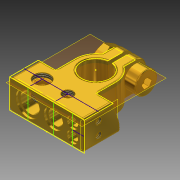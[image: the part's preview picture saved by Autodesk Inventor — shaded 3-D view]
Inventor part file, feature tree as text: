
AUTODESK INVENTOR PART (.ipt)
format: ipt  version: 2014 (Build 180170000, 170)  size: 792,576 bytes
history: native  units: in
note: dims shown in document units (in); Inventor stores cm internally (conversion verified against a paired STEP export)
features: sketch x14, projected_geometry x13, fillet x11, extrude x9, hole x7, other x6, chamfer x4, plane x3, surface_op x2, thread x2, mirror x1
ambient origin geometry x8: Origin, YZ Plane, XZ Plane, XY Plane, X Axis, Y Axis, Z Axis, Center Point
bodies: Solid1 (feature_tree)
feature tree (72):
  sketch  "Sketch1"  dims[d0=0.125in d2=0.375in]
  sketch  "Sketch2"  dims[d3=0.625in d4=0.5in d5=0.125in]
  plane  "Work Plane1"
  extrude  "Extrusion1"  Depth=0.125in
  surface_op  "Sculpt1"
  hole  "Hole1"  [1 undecoded]
  fillet  "Fillet1"  Radius=0.125in
  sketch  "Sketch4"  dims[d10=0.125in d11=1.0in d12=0.0in]
  hole  "Hole2"  [1 undecoded]
  hole  "Hole3"  [1 undecoded]
  hole  "Hole4"  [1 undecoded]
  extrude  "Extrusion3"  Depth=0.05in
  extrude  "Extrusion4"  Depth=0.03in
  mirror  "Mirror1"
  sketch  "Sketch8"  dims[d30=0.32in d31=0.75in d32=0.375in d33=0.25in d34=0.5635in d35=0.5in d36=0.0in]
  hole  "Hole5"  [1 undecoded]
  hole  "Hole6"  [1 undecoded]
  hole  "Hole7"  [1 undecoded]
  fillet  "Fillet3"  Radius=0.075in
  fillet  "Fillet4"  Radius=0.075in
  fillet  "Fillet5"  Radius=0.025in
  fillet  "Fillet6"  Radius=0.025in
  fillet  "Fillet7"  Radius=0.05in
  fillet  "Fillet8"  Radius=0.025in
  surface_op  "Sculpt2"
  extrude  "Extrusion5"  Depth=0.125in TaperAngle=0.0deg
  fillet  "Fillet9"  Radius=0.125in
  extrude  "Extrusion6"  [1 undecoded]
  chamfer  "Chamfer1"  Distance=0.28in
  plane  "Work Plane2"
  extrude  "Extrusion7"  Depth=0.125in TaperAngle=0.0deg
  thread  "Thread1"  [1 undecoded]
  thread  "Thread2"  [1 undecoded]
  chamfer  "Chamfer2"  Distance=0.1in
  extrude  "Extrusion8"  Depth=0.125in
  fillet  "Fillet10"  Radius=0.025in
  fillet  "Fillet11"  [1 undecoded]
  plane  "Work Plane3"
  extrude  "Extrusion9"  Depth=0.125in TaperAngle=0.0deg
  extrude  "Extrusion10"  Depth=0.125in
  fillet  "Fillet12"  Radius=0.075in
  chamfer  "Chamfer3"  Distance=0.125in
  chamfer  "Chamfer4"  Distance=0.01in
  sketch  "Sketch3"  dims[d8=0.0938in d9=0.1875in]
  projected_geometry  "Projected Loop1"
  projected_geometry  "Projected Loop2"
  sketch  "Sketch6"  dims[d13=0.25in d14=0.75in d15=0.375in d16=0.25in d17=0.5635in d18=1.0in d19=0.8108in d20=0.25in]
  sketch  "Sketch7"  dims[d23=0.425in d24=0.75in d25=0.375in d26=0.25in d27=0.5635in d28=0.5in d29=0.0in]
  projected_geometry  "Projected Loop4"
  projected_geometry  "Projected Loop5"
  projected_geometry  "Projected Loop6"
  projected_geometry  "Projected Loop7"
  sketch  "Sketch9"  dims[d37=0.1875in d38=0.75in d39=0.375in d40=0.25in d41=0.5635in d42=0.5in d43=0.0in d50=0.05in]
  projected_geometry  "Projected Loop8"
  projected_geometry  "Projected Loop9"
  projected_geometry  "Projected Loop10"
  sketch  "Sketch10"  dims[d51=0.05in d52=0.03in]
  sketch  "Sketch11"  dims[d53=0.03in d54=0.05in d55=0.0in]
  projected_geometry  "Projected Loop11"
  sketch  "Sketch12"  dims[d56=0.05in d57=0.0in]
  sketch  "Sketch13"  dims[d58=0.336in d59=0.75in d60=0.375in d61=0.25in d62=0.5635in d63=0.375in d64=0.0in]
  projected_geometry  "Projected Loop12"
  sketch  "Sketch14"  dims[d65=0.216in d66=0.75in d67=0.375in d68=0.25in d69=0.5635in d70=0.375in d71=0.0in]
  sketch  "Sketch15"  dims[d72=0.13in d73=0.75in d74=0.375in d75=0.25in d76=0.5635in d77=0.25in d78=0.0in d79=0.0625in d80=0.5in d81=0.075in d82=0.075in d83=0.025in d84=0.025in d85=0.05in d86=0.0in d87=0.025in d88=0.14in d89=0.0in d90=0.02in d91=0.125in d92=45.0deg d93=-0.09in d94=0.28in d95=0.0in d96=1.0in d97=0.0in d98=1.0in d99=0.0in d100=0.025in d101=0.125in d102=45.0deg d103=0.1in d104=0.0in d105=0.025in d106=0.025in d107=-0.0625in d108=0.225in d109=0.0in d110=0.075in d111=0.075in d112=0.125in d113=0.0in d114=0.01in d115=0.005in d116=0.125in d117=45.0deg d118=0.025in d119=0.125in d120=45.0deg]
  projected_geometry  "Projected Loop13"
  projected_geometry  "Projected Loop14"
  other  "Composite1"
  other  "Srf1"
  other  "Composite2"
  other  "Srf2"
  other  "Composite3"
  other  "Srf3"
note: 11 required parameter values undecoded (feature->parameter linkage not recoverable at this tier; creation-order binding heuristic only, values carry confidence <= 0.55)
